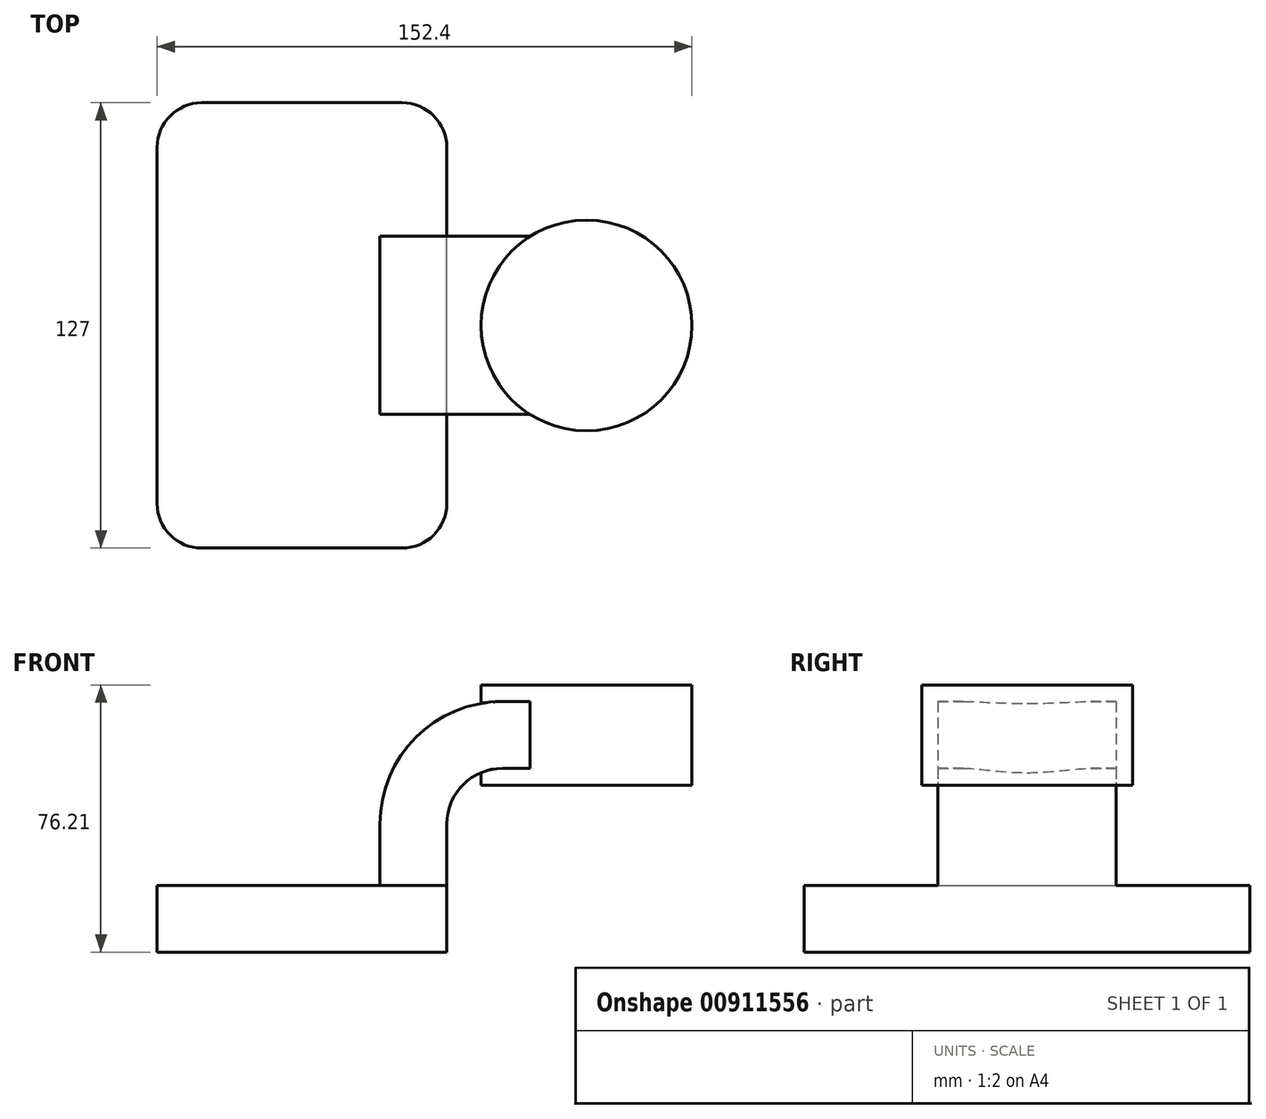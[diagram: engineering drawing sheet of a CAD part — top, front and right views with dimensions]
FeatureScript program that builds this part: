
annotation { "Feature Type Name" : "Feature", "Feature Type Description" : "" }
export const myFeature = defineFeature(function(context is Context, id is Id, definition is map)
    precondition{}
    {
        {
            var Q0;
            Q0=qCreatedBy(makeId("Front.planeOp"),FACE);
            var sketch = newSketch(context, id + "F0", { "sketchPlane" : qUnion([Q0])});
            skLineSegment(sketch, "E0.bottom", {"start": v(41.28, -9.52) * mm, "end": v(-41.28, -9.53) * mm});
            skLineSegment(sketch, "E0.top", {"start": v(41.28, 9.53) * mm, "end": v(-41.28, 9.53) * mm});
            skLineSegment(sketch, "E0.left", {"start": v(41.28, -9.52) * mm, "end": v(41.28, 9.53) * mm});
            skLineSegment(sketch, "E0.right", {"start": v(-41.28, -9.53) * mm, "end": v(-41.28, 9.53) * mm});
            skPoint(sketch, "E0.middle", {"position": v(0, 0) * mm});
            skLineSegment(sketch, "E1.bottom", {"start": v(111.12, 38.1) * mm, "end": v(60.32, 38.1) * mm});
            skLineSegment(sketch, "E1.top", {"start": v(111.12, 66.68) * mm, "end": v(60.33, 66.68) * mm});
            skLineSegment(sketch, "E1.left", {"start": v(111.12, 38.1) * mm, "end": v(111.12, 66.68) * mm});
            skLineSegment(sketch, "E1.right", {"start": v(60.32, 38.1) * mm, "end": v(60.32, 66.68) * mm});
            skPoint(sketch, "E1.middle", {"position": v(85.72, 52.39) * mm});
            skLineSegment(sketch, "E2", {"start": v(41.28, 9.53) * mm, "end": v(41.28, 27) * mm});
            skArc(sketch, "E3", {"start": v(41.27, 27) * mm, "mid": v(45.92, 38.23) * mm, "end": v(57.15, 42.88) * mm});
            skLineSegment(sketch, "E4", {"start": v(57.15, 42.88) * mm, "end": v(81.09, 42.88) * mm});
            skLineSegment(sketch, "E5.0", {"start": v(57.15, 61.93) * mm, "end": v(81.09, 61.93) * mm});
            skArc(sketch, "E5.1", {"start": v(22.23, 27) * mm, "mid": v(32.45, 51.7) * mm, "end": v(57.15, 61.93) * mm});
            skLineSegment(sketch, "E5.2", {"start": v(22.22, 9.53) * mm, "end": v(22.22, 27) * mm});
            skLineSegment(sketch, "E6", {"start": v(81.09, 42.88) * mm, "end": v(81.09, 61.93) * mm});
            skFitSpline(sketch, "E7", {"points": [v(-41.28, 9.53) * mm, v(57.15, 61.93) * mm], "startDerivative": vector(111.74, 19.87) * mm, "endDerivative": vector(118.24, -1.63) * mm});
            skLineSegment(sketch, "E8", {"start": v(81.09, 42.88) * mm, "end": v(81.09, 38.1) * mm});
            skLineSegment(sketch, "E9", {"start": v(81.09, 38.1) * mm, "end": v(81.09, 66.68) * mm});
            skSolve(sketch);
        }
        {
            var Q0;
            Q0=makeQuery(id+"F0.imprint","IMPRINT",FACE,{"disambiguationData":[TD([[makeQuery(id+"F0.imprint","IMPRINT",EDGE,{"derivedFrom":sQuery(id+"F0.wireOp",EDGE,"E0.bottom")}),-1.0]])]});
            extrude(context, id + "F1", {"entities" : qUnion([Q0]), "endBound" : BoundingType.SYMMETRIC, "depth" : 127 * mm, "offsetDistance" : 25.4 * mm});
        }
        {
            var Q0;
            {var subQ1=sQuery(id+"F0.wireOp",EDGE,"E2");Q0=makeQuery(id+"F0.imprint","IMPRINT",FACE,{"disambiguationData":[TD([[makeQuery(id+"F0.imprint","IMPRINT",EDGE,{"derivedFrom":subQ1}),1.0]])]});}
            var Q1;
            {var subQ5=sQuery(id+"F0.wireOp",EDGE,"E6");Q1=makeQuery(id+"F0.imprint","IMPRINT",FACE,{"disambiguationData":[TD([[makeQuery(id+"F0.imprint","IMPRINT",EDGE,{"derivedFrom":subQ5}),1.0]])]});}
            var Q2;
            {var subQ0=sQuery(id+"F0.wireOp",EDGE,"E4");var subQ1=sQuery(id+"F0.wireOp",EDGE,"E1.right");var subQ2=makeQuery(id+"F0.imprint","INTERSECT",VERTEX,{"derivedFrom":[subQ1,subQ0]});Q2=makeQuery(id+"F0.imprint","IMPRINT",FACE,{"disambiguationData":[TD([[makeQuery(id+"F0.imprint","IMPRINT",EDGE,{"disambiguationData":[TD([[subQ2,-1.0]])],"derivedFrom":subQ1}),-1.0]])]});}
            extrude(context, id + "F2", {"entities" : qUnion([Q0, Q1, Q2]), "operationType" : NewBodyOperationType.ADD, "endBound" : BoundingType.SYMMETRIC, "depth" : 50.8 * mm, "offsetDistance" : 25.4 * mm});
        }
        {
            var Q0;
            Q0=makeQuery(id+"F0.imprint","IMPRINT",FACE,{"disambiguationData":[TD([[makeQuery(id+"F0.imprint","IMPRINT",EDGE,{"derivedFrom":sQuery(id+"F0.wireOp",EDGE,"E5.1")}),1.0]])]});
            extrude(context, id + "F3", {"entities" : qUnion([Q0]), "operationType" : NewBodyOperationType.ADD, "endBound" : BoundingType.SYMMETRIC, "depth" : 12.7 * mm, "offsetDistance" : 25.4 * mm});
        }
        {
            var Q0;
            {var subQ0=sQuery(id+"F0.wireOp",EDGE,"E1.left");Q0=makeQuery(id+"F0.imprint","IMPRINT",FACE,{"disambiguationData":[TD([[makeQuery(id+"F0.imprint","IMPRINT",EDGE,{"derivedFrom":subQ0}),1.0]])]});}
            var Q1;
            Q1=sQuery(id+"F0.wireOp",EDGE,"E6");
            revolve(context, id + "F4", {"operationType" : NewBodyOperationType.ADD, "surfaceOperationType" : NewSurfaceOperationType.NEW, "entities" : qUnion([Q0]), "axis" : qUnion([Q1]), "revolveType" : RevolveType.FULL});
        }
        {
            var Q0;
            Q0=makeQuery(id+"F1.opExtrude","CAP_EDGE",EDGE,{"disambiguationData":[OSD([sQuery(id+"F0.wireOp",EDGE,"E0.right")])],"isStart":true});
            var Q1;
            Q1=makeQuery(id+"F1.opExtrude","CAP_EDGE",EDGE,{"disambiguationData":[OSD([sQuery(id+"F0.wireOp",EDGE,"E0.right")])],"isStart":false});
            var Q2;
            Q2=makeQuery(id+"F1.opExtrude","CAP_EDGE",EDGE,{"disambiguationData":[OSD([sQuery(id+"F0.wireOp",EDGE,"E0.left")])],"isStart":false});
            var Q3;
            Q3=makeQuery(id+"F1.opExtrude","CAP_EDGE",EDGE,{"disambiguationData":[OSD([sQuery(id+"F0.wireOp",EDGE,"E0.left")])],"isStart":true});
            fillet(context, id + "F5", {"entities" : qUnion([Q0, Q1, Q2, Q3]), "radius" : 12.7 * mm, "tangentPropagation" : true, "allowEdgeOverflow" : false});
        }
    });
